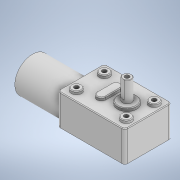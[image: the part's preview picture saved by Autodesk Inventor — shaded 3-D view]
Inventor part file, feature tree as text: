
AUTODESK INVENTOR PART (.ipt)
format: ipt  version: 2020.2 (Build 242310000, 310)  size: 317,952 bytes
history: native  units: mm
features: extrude x8, sketch x8, chamfer x5, thread x5, fillet x3
ambient origin geometry x8: Origin, YZ Plane, XZ Plane, XY Plane, X Axis, Y Axis, Z Axis, Center Point
bodies: Solid1 (feature_tree)
feature tree (29):
  extrude  "Extrusion1"  Depth=46.0mm
  chamfer  "Chamfer1"  Distance=22.0mm
  chamfer  "Chamfer2"  Distance=1.0mm Angle=45.0deg
  chamfer  "Chamfer3"  Distance=1.0mm Angle=45.0deg
  chamfer  "Chamfer4"  Distance=1.0mm Angle=45.0deg
  fillet  "Fillet1"  Radius=2.0mm
  extrude  "Extrusion2"  Depth=3.0mm
  fillet  "Fillet2"  Radius=6.5mm
  extrude  "Extrusion3"  Depth=7.0mm
  extrude  "Extrusion4"  Depth=3.0mm
  chamfer  "Chamfer5"  Distance=2.0mm
  thread  "Thread1"  [1 undecoded]
  thread  "Thread2"  [1 undecoded]
  thread  "Thread3"  [1 undecoded]
  thread  "Thread4"  [1 undecoded]
  thread  "Thread5"  [1 undecoded]
  extrude  "Extrusion5"  Depth=10.0mm
  extrude  "Extrusion6"  Depth=0.5mm
  extrude  "Extrusion7"  Depth=0.5mm
  extrude  "Extrusion8"  Depth=6.0mm
  fillet  "Fillet3"  Radius=3.0mm
  sketch  "Sketch1"  dims[d0=32.0mm d1=46.0mm d2=22.0mm d3=0.0mm d4=1.0mm d5=5.0mm d6=45.0deg d7=1.0mm d8=5.0mm d9=45.0deg d10=1.0mm d11=5.0mm d12=45.0deg]
  sketch  "Sketch2"  dims[d13=1.0mm d14=5.0mm d15=45.0deg d16=2.0mm]
  sketch  "Sketch3"  dims[d17=7.0mm d18=3.0mm d19=6.5mm]
  sketch  "Sketch4"  dims[d20=6.5mm d21=7.0mm]
  sketch  "Sketch5"  dims[d22=3.0mm d23=6.5mm]
  sketch  "Sketch6"  dims[d24=5.5mm d25=2.0mm d26=0.0mm d27=13.0mm d28=14.5mm d29=32.0mm d30=16.0mm d31=6.0mm]
  sketch  "Sketch7"  dims[d32=3.0mm d33=10.0mm]
  sketch  "Sketch8"  dims[d34=5.0mm d35=9.5mm d36=0.5mm d37=6.0mm d38=3.0mm d39=14.0mm d40=0.0mm d41=5.5mm d42=12.0mm d43=0.0mm d44=0.3mm d45=5.0mm d46=45.0deg d47=2.0mm d48=0.0mm d49=2.0mm d50=0.0mm d51=2.0mm d52=0.0mm d53=2.0mm d54=0.0mm d55=14.0mm d56=0.0mm d57=24.0mm d58=12.0mm d59=0.5mm d60=31.0mm d61=0.0mm d62=0.5mm d63=0.5mm d64=0.0mm d65=6.5mm d66=3.0mm d67=0.0mm d68=0.5mm d69=13.0mm d70=3.0mm d71=22.0mm d72=11.0mm d73=0.5mm d74=0.0mm]
note: 5 required parameter values undecoded (feature->parameter linkage not recoverable at this tier; creation-order binding heuristic only, values carry confidence <= 0.55)
